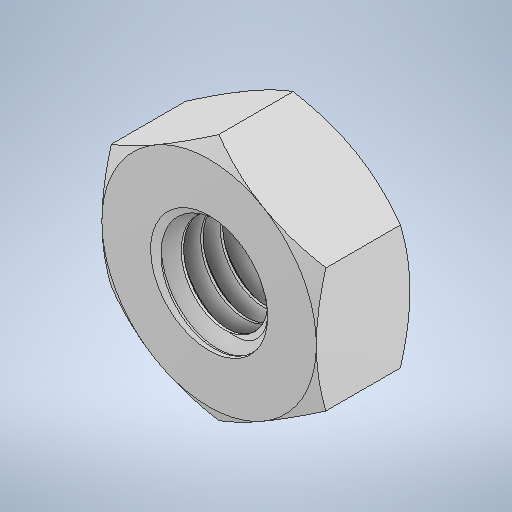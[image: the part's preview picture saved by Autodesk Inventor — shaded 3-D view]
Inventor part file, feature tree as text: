
AUTODESK INVENTOR PART (.ipt)
format: ipt  version: 2025 (Build 290162000, 162)  size: 370,176 bytes
history: native  units: in
note: dims shown in document units (in); Inventor stores cm internally (conversion verified against a paired STEP export)
features: mirror x1
ambient origin geometry x8: Origin, YZ Plane, XZ Plane, XY Plane, X Axis, Y Axis, Z Axis, Center Point
bodies: Solid1 (feature_tree)
feature tree (1):
  mirror  "Mirror2"
